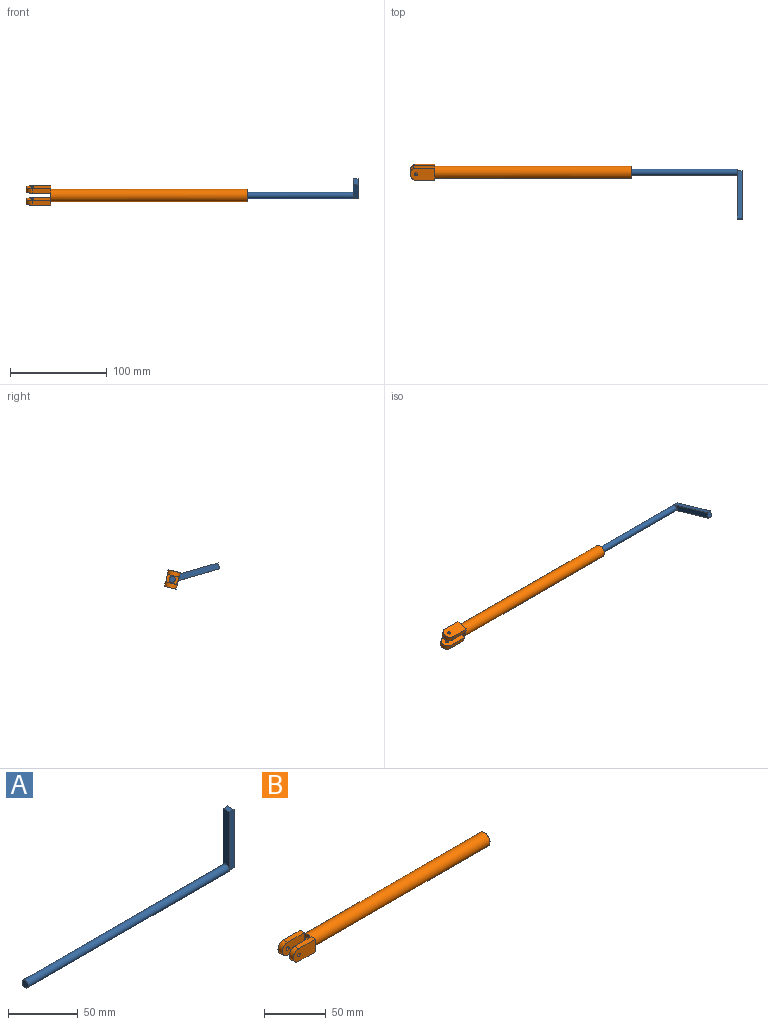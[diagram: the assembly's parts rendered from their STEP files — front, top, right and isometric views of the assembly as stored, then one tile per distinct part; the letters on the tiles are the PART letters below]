
ASSEMBLY  parts=2 mates=1
PART A: 10 faces, bbox 208x6.4x53.3 mm
  f0: plane 1.34x0.07mm, normal (1,0,0), area 0.1mm2, adj f1,f5
  f1: cylinder r=3.17mm len=203.2mm, axis (-1,0,0), area 4053.7mm2, adj f0,f2,f3,f4
  f2: plane 6.21x2.51mm, normal (1,0,0), area 11.6mm2, adj f1,f6
  f3: plane 6.35x6.35mm, normal (-1,0,0), area 31.7mm2, adj f1
  f4: plane 50.8x6.35mm, normal (-1,0,0), area 302.6mm2, adj f1,f5,f6,f7,f8
  f5: plane 50.8x4.76mm, normal (0,-1,0), area 241.9mm2, adj f0,f4,f6,f8,f9
  f6: plane 6.35x4.76mm, normal (0,0,-1), area 30.2mm2, adj f2,f4,f5,f7,f9
  f7: plane 50.8x4.76mm, normal (0,1,0), area 241.9mm2, adj f4,f6,f8,f9
  f8: plane 6.35x4.76mm, normal (0,0,1), area 30.2mm2, adj f4,f5,f7,f9
  f9: plane 50.8x6.35mm, normal (1,0,0), area 322.6mm2, adj f5,f6,f7,f8
PART B: 18 faces, bbox 228.6x17.5x12.7 mm
  f0: plane 12.7x7.94mm, normal (-1,0,0), area 62.1mm2, adj f1,f2,f4,f10
  f1: cylinder r=3.17mm len=203.2mm, axis (-1,0,0), area 4053.7mm2, adj f0,f3
  f2: cylinder r=6.35mm len=203.2mm, axis (-1,0,0), area 8107.3mm2, adj f0,f3,f8,f9
  f3: plane 12.7x12.7mm, normal (1,0,0), area 95mm2, adj f1,f2
  f4: plane 25.4x12.7mm, normal (0,-1,0), area 297.4mm2, adj f0,f5,f7,f8,f15,f17
  f5: plane 19.05x4.76mm, normal (0,0,1), area 90.7mm2, adj f4,f6,f8,f17
  f6: plane 25.4x12.7mm, normal (0,1,0), area 297.4mm2, adj f5,f7,f8,f15,f17
  f7: plane 19.05x4.76mm, normal (0,0,-1), area 90.7mm2, adj f4,f6,f8,f17
  f8: plane 12.7x4.76mm, normal (1,0,0), area 44mm2, adj f2,f4,f5,f6,f7
  f9: plane 12.7x4.76mm, normal (1,0,0), area 44mm2, adj f2,f10,f11,f12,f13
  f10: plane 25.4x12.7mm, normal (0,1,0), area 297.4mm2, adj f0,f9,f11,f13,f14,f16
  f11: plane 19.05x4.76mm, normal (0,0,-1), area 90.7mm2, adj f9,f10,f12,f16
  f12: plane 25.4x12.7mm, normal (0,-1,0), area 297.4mm2, adj f9,f11,f13,f14,f16
  f13: plane 19.05x4.76mm, normal (0,0,1), area 90.7mm2, adj f9,f10,f12,f16
  f14: cylinder r=1.59mm len=4.76mm, axis (0,-1,0), area 47.5mm2, adj f10,f12
  f15: cylinder r=1.59mm len=4.76mm, axis (0,-1,0), area 47.5mm2, adj f4,f6
  f16: cylinder r=6.35mm len=12.7mm, axis (0,-1,0), area 95mm2, adj f10,f11,f12,f13
  f17: cylinder r=6.35mm len=12.7mm, axis (0,1,0), area 95mm2, adj f4,f5,f6,f7
PLACE A rot(axis=(1,0,0),73.8deg) t=(32.41,6.78,33.65)mm fixed
PLACE B rot(axis=(-1,0,0),76.5deg) t=(-76.59,15.14,-49.65)mm
MATE cylindrical B.f1 <-> A.f1  axis (-1,0,0) through (126.61,-0.08,-0.23)mm
